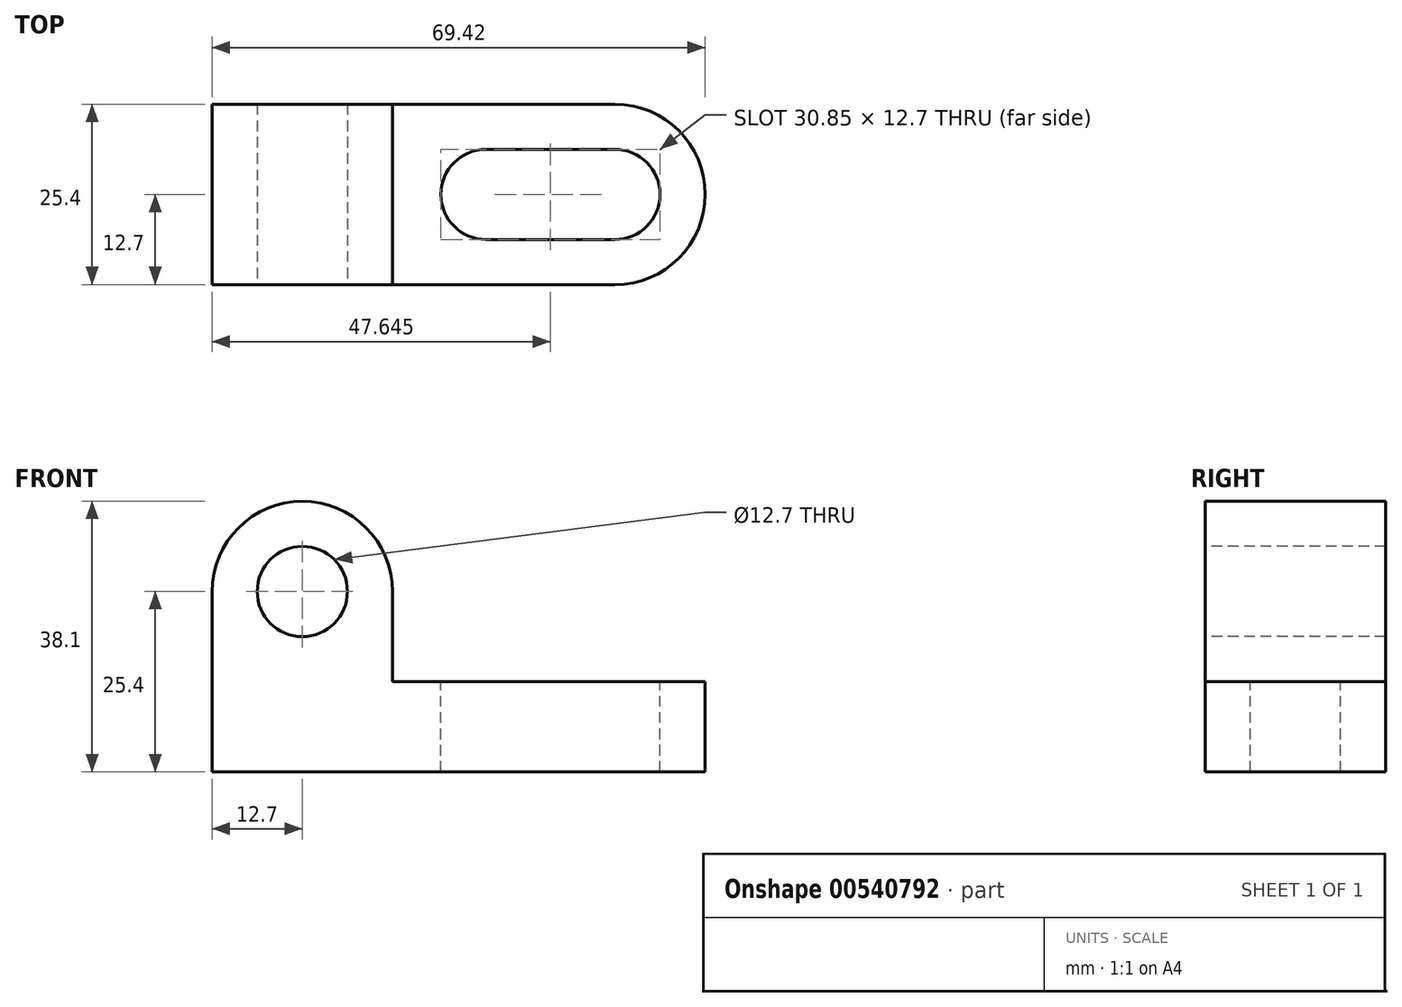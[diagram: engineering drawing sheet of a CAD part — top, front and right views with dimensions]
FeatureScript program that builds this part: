
annotation { "Feature Type Name" : "Feature", "Feature Type Description" : "" }
export const myFeature = defineFeature(function(context is Context, id is Id, definition is map)
    precondition{}
    {
        {
            var Q0;
            Q0=qCreatedBy(makeId("Front.planeOp"),FACE);
            var sketch = newSketch(context, id + "F0", { "sketchPlane" : qUnion([Q0])});
            skLineSegment(sketch, "E0", {"start": v(0, 0) * mm, "end": v(69.85, 0) * mm});
            skLineSegment(sketch, "E1", {"start": v(69.85, 0) * mm, "end": v(69.85, 12.7) * mm});
            skLineSegment(sketch, "E2", {"start": v(69.85, 12.7) * mm, "end": v(25.4, 12.7) * mm});
            skLineSegment(sketch, "E3", {"start": v(25.4, 12.7) * mm, "end": v(25.4, 38.1) * mm});
            skLineSegment(sketch, "E4", {"start": v(25.4, 38.1) * mm, "end": v(0, 38.1) * mm});
            skLineSegment(sketch, "E5", {"start": v(0, 38.1) * mm, "end": v(0, 0) * mm});
            skSolve(sketch);
        }
        {
            var Q0;
            Q0=makeQuery(id+"F0.imprint","IMPRINT",FACE,{"disambiguationData":[TD([[makeQuery(id+"F0.imprint","IMPRINT",EDGE,{"derivedFrom":sQuery(id+"F0.wireOp",EDGE,"E0")}),1.0]])]});
            extrude(context, id + "F1", {"entities" : qUnion([Q0]), "depth" : 25.4 * mm, "offsetDistance" : 25.4 * mm});
        }
        {
            var Q0;
            Q0=makeQuery(id+"F1.opExtrude","CAP_FACE",FACE,{"disambiguationData":[OSD([sQuery(id+"F0.wireOp",EDGE,"E0"),sQuery(id+"F0.wireOp",EDGE,"E1"),sQuery(id+"F0.wireOp",EDGE,"E2"),sQuery(id+"F0.wireOp",EDGE,"E3"),sQuery(id+"F0.wireOp",EDGE,"E4"),sQuery(id+"F0.wireOp",EDGE,"E5")])],"isStart":false});
            var sketch = newSketch(context, id + "F2", { "sketchPlane" : qUnion([Q0])});
            skCircle(sketch, "E6", {"center": v(12.7, 25.4) * mm, "radius": 6.35 * mm});
            skArc(sketch, "E7", {"start": v(25.4, 25.4) * mm, "mid": v(12.7, 38.1) * mm, "end": v(0, 25.4) * mm});
            skSolve(sketch);
        }
        {
            var Q0;
            Q0=makeQuery(id+"F2.imprint","IMPRINT",FACE,{"disambiguationData":[TD([[makeQuery(id+"F2.imprint","IMPRINT",EDGE,{"derivedFrom":sQuery(id+"F2.wireOp",EDGE,"E6")}),1.0]])]});
            var Q1;
            {var subQ0=sQuery(id+"F2.wireOp",EDGE,"E7");var subQ1=makeQuery(id+"F1.opExtrude","CAP_EDGE",EDGE,{"disambiguationData":[OSD([sQuery(id+"F0.wireOp",EDGE,"E3")])],"isStart":false});var subQ2=makeQuery(id+"F2.imprint","INTERSECT",VERTEX,{"derivedFrom":[subQ1,subQ0]});Q1=makeQuery(id+"F2.imprint","IMPRINT",FACE,{"disambiguationData":[TD([[makeQuery(id+"F2.imprint","IMPRINT",EDGE,{"disambiguationData":[TD([[subQ2,-1.0]])],"derivedFrom":subQ0}),-1.0]])]});}
            var Q2;
            {var subQ0=sQuery(id+"F2.wireOp",EDGE,"E7");var subQ1=makeQuery(id+"F1.opExtrude","CAP_EDGE",EDGE,{"disambiguationData":[OSD([sQuery(id+"F0.wireOp",EDGE,"E5")])],"isStart":false});var subQ2=makeQuery(id+"F2.imprint","INTERSECT",VERTEX,{"derivedFrom":[subQ1,subQ0]});Q2=makeQuery(id+"F2.imprint","IMPRINT",FACE,{"disambiguationData":[TD([[makeQuery(id+"F2.imprint","IMPRINT",EDGE,{"disambiguationData":[TD([[subQ2,1.0]])],"derivedFrom":subQ0}),-1.0]])]});}
            extrude(context, id + "F3", {"entities" : qUnion([Q0, Q1, Q2]), "operationType" : NewBodyOperationType.REMOVE, "oppositeDirection" : true, "depth" : 25.4 * mm, "offsetDistance" : 25.4 * mm});
        }
        {
            var Q0;
            Q0=makeQuery(id+"F1.opExtrude","SWEPT_FACE",FACE,{"disambiguationData":[OSD([sQuery(id+"F0.wireOp",EDGE,"E2")])]});
            var sketch = newSketch(context, id + "F4", { "sketchPlane" : qUnion([Q0])});
            skCircle(sketch, "E8", {"center": v(56.72, -12.7) * mm, "radius": 6.35 * mm});
            skCircle(sketch, "E9", {"center": v(38.57, -12.7) * mm, "radius": 6.35 * mm});
            skArc(sketch, "E10", {"start": v(56.72, -25.4) * mm, "mid": v(69.42, -12.7) * mm, "end": v(56.72, 0) * mm});
            skLineSegment(sketch, "E11", {"start": v(56.72, -19.05) * mm, "end": v(38.57, -19.05) * mm});
            skLineSegment(sketch, "E12", {"start": v(56.72, -6.35) * mm, "end": v(38.57, -6.35) * mm});
            skSolve(sketch);
        }
        {
            var Q0;
            {var subQ0=sQuery(id+"F4.wireOp",EDGE,"E9");var subQ1=makeQuery(id+"F4.imprint","INTERSECT",VERTEX,{"derivedFrom":[subQ0,sQuery(id+"F4.wireOp",EDGE,"E11")]});Q0=makeQuery(id+"F4.imprint","IMPRINT",FACE,{"disambiguationData":[TD([[makeQuery(id+"F4.imprint","IMPRINT",EDGE,{"disambiguationData":[TD([[subQ1,1.0]])],"derivedFrom":subQ0}),1.0]])]});}
            var Q1;
            {var subQ0=sQuery(id+"F4.wireOp",EDGE,"E11");Q1=makeQuery(id+"F4.imprint","IMPRINT",FACE,{"disambiguationData":[TD([[makeQuery(id+"F4.imprint","IMPRINT",EDGE,{"derivedFrom":subQ0}),-1.0]])]});}
            var Q2;
            {var subQ0=sQuery(id+"F4.wireOp",EDGE,"E8");var subQ1=makeQuery(id+"F4.imprint","INTERSECT",VERTEX,{"derivedFrom":[subQ0,sQuery(id+"F4.wireOp",EDGE,"E11")]});Q2=makeQuery(id+"F4.imprint","IMPRINT",FACE,{"disambiguationData":[TD([[makeQuery(id+"F4.imprint","IMPRINT",EDGE,{"disambiguationData":[TD([[subQ1,1.0]])],"derivedFrom":subQ0}),1.0]])]});}
            var Q3;
            {var subQ0=sQuery(id+"F4.wireOp",EDGE,"E10");Q3=makeQuery(id+"F4.imprint","IMPRINT",FACE,{"disambiguationData":[TD([[makeQuery(id+"F4.imprint","IMPRINT",EDGE,{"derivedFrom":subQ0}),-1.0]])]});}
            extrude(context, id + "F5", {"entities" : qUnion([Q0, Q1, Q2, Q3]), "operationType" : NewBodyOperationType.REMOVE, "oppositeDirection" : true, "depth" : 12.7 * mm, "offsetDistance" : 25.4 * mm});
        }
    });
